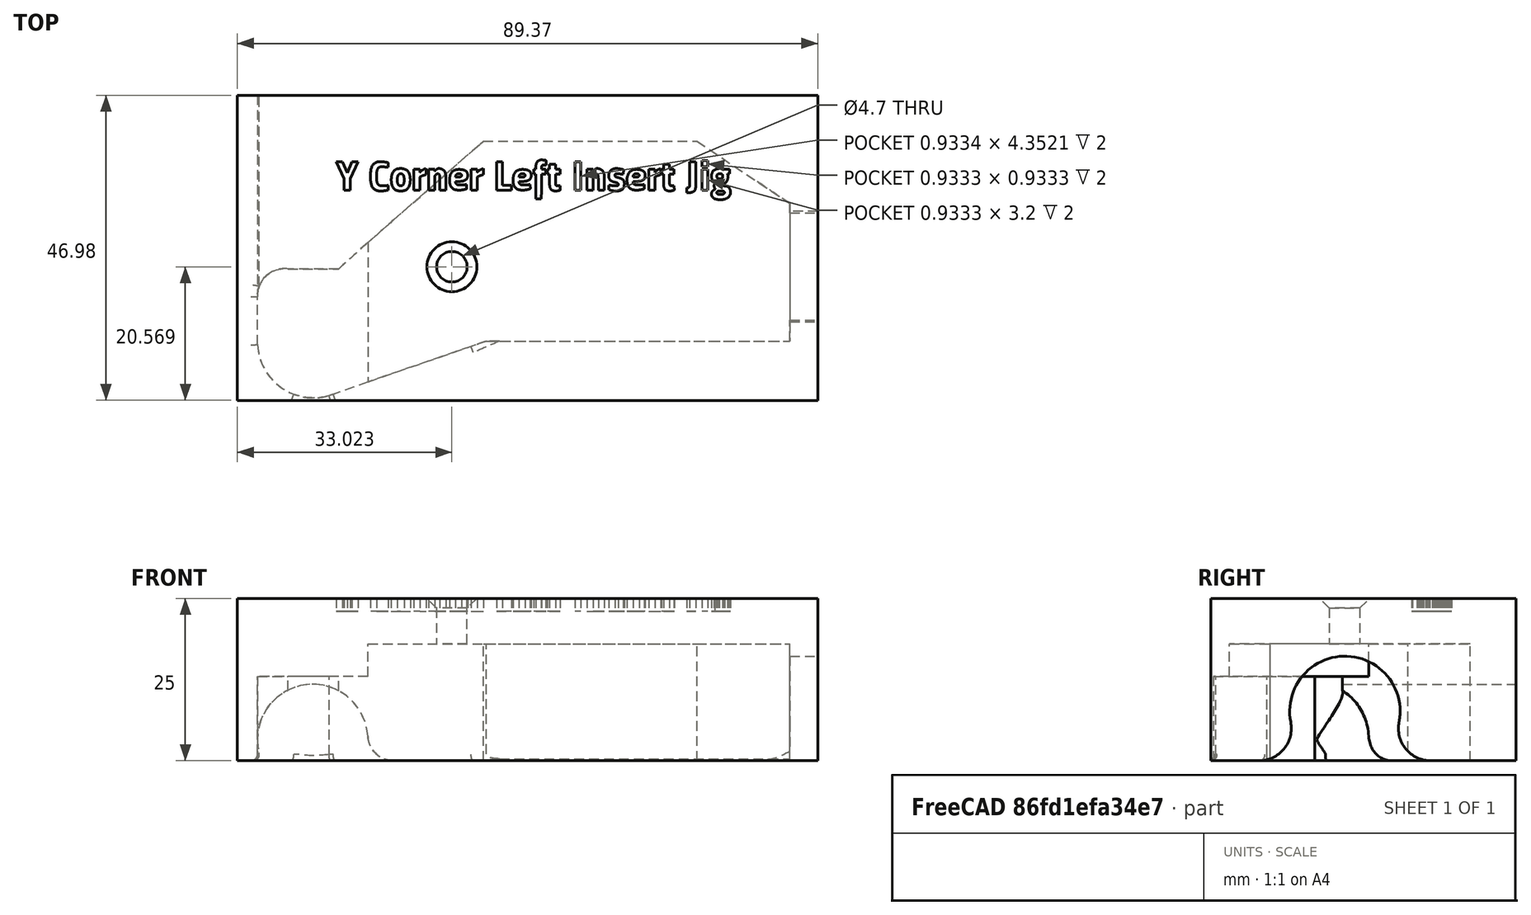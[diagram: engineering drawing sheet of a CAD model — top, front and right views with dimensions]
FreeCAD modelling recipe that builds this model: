
FCSTD DOCUMENT  (FreeCAD 0.17R9537 (Git))
Label: y_corner_left_insert_jig_m3
License: All rights reserved
LicenseURL: http://en.wikipedia.org/wiki/All_rights_reserved
objects: Sketcher::SketchObject×8, PartDesign::Pocket×6, PartDesign::Fillet×3, Mesh::Feature×1, PartDesign::Pad×1, Part::Feature×1, PartDesign::Plane×1, PartDesign::Chamfer×1, Part::Part2DObjectPython×1, PartDesign::Body×1
note: 30 computed .brp shape members not serialized (recipe doc carries the construction recipe); baked Part::Feature solids carry a one-line shape summary decoded from their .brp

FEATURE [Mesh::Feature] y_corner_left_v2_4  label="y_corner_left_v2.4"
  Placement = pos=(-95,-15,-13) rot=(0,0,1;0rad)
FEATURE [Sketcher::SketchObject] Sketch
  MapMode = 5
  Support = -> [XY_Plane]
  sketch-geometry (4):
    g0: LineSegment StartX=-41.2454 StartY=-29.3641 StartZ=0 EndX=48.1248 EndY=-29.3641 EndZ=0
    g1: LineSegment StartX=48.1248 StartY=-29.3641 StartZ=0 EndX=48.1248 EndY=17.6233 EndZ=0
    g2: LineSegment StartX=48.1248 StartY=17.6233 StartZ=0 EndX=-41.2454 EndY=17.6233 EndZ=0
    g3: LineSegment StartX=-41.2454 StartY=17.6233 StartZ=0 EndX=-41.2454 EndY=-29.3641 EndZ=0
  constraints (8):
    c: Coincident(g0,g1)
    c: Coincident(g1,g2)
    c: Coincident(g2,g3)
    c: Coincident(g3,g0)
    c: Horizontal(g0)
    c: Horizontal(g2)
    c: Vertical(g1)
    c: Vertical(g3)
FEATURE [PartDesign::Pad] Pad
  Length = 25
  Length2 = 100
  Profile = -> Sketch
  Type = 0
FEATURE [Part::Feature] y_corner_left_v2_4001
  Placement = pos=(0,0,12) rot=(0,0,1;0rad)
  shape: bbox 81.06 x 37.98 x 18.29 mm, 18592 faces, 0 solids (baked)
FEATURE [Sketcher::SketchObject] Sketch001
  MapMode = 5
  Placement = pos=(0,0,0) rot=(1,0,0;3.14159rad)
  Support = -> [Pad]
  sketch-geometry (7):
    g0: LineSegment StartX=-21.1438 StartY=5.05934 StartZ=0 EndX=-3.38972 EndY=-10.5427 EndZ=0
    g1: LineSegment StartX=-3.38972 StartY=-10.5427 StartZ=0 EndX=29.5098 EndY=-10.5427 EndZ=0
    g2: LineSegment StartX=29.5098 StartY=-10.5427 StartZ=0 EndX=43.8429 EndY=-0.932231 EndZ=0
    g3: LineSegment StartX=43.8429 StartY=-0.932231 StartZ=0 EndX=43.8429 EndY=20.2526 EndZ=0
    g4: LineSegment StartX=-21.1438 StartY=5.05934 StartZ=0 EndX=-21.1438 EndY=26.5193 EndZ=0
    g5: LineSegment StartX=-21.1438 StartY=26.5193 StartZ=0 EndX=-2.94605 EndY=20.2526 EndZ=0
    g6: LineSegment StartX=-2.94605 StartY=20.2526 StartZ=0 EndX=43.8429 EndY=20.2526 EndZ=0
  constraints (11):
    c: Coincident(g1,g0)
    c: Horizontal(g1)
    c: Coincident(g2,g1)
    c: Coincident(g3,g2)
    c: Vertical(g3)
    c: Coincident(g4,g0)
    c: Vertical(g4)
    c: Coincident(g5,g4)
    c: Coincident(g6,g5)
    c: Coincident(g6,g3)
    c: Horizontal(g6)
FEATURE [PartDesign::Pocket] Pocket
  BaseFeature = -> Pad
  Length = 18
  Profile = -> Sketch001
  Type = 0
FEATURE [Sketcher::SketchObject] Sketch002
  ExternalGeometry = -> [Pocket]
  MapMode = 5
  Placement = pos=(0,0,0) rot=(1,0,0;3.14159rad)
  Support = -> [Pocket]
  sketch-geometry (7):
    g0: LineSegment StartX=-21.1438 StartY=5.05934 StartZ=0 EndX=-25.6743 EndY=9.11448 EndZ=0
    g1: LineSegment StartX=-25.6743 StartY=9.11448 StartZ=0 EndX=-33.4497 EndY=9.11448 EndZ=0
    g2: LineSegment StartX=-21.1438 StartY=26.5193 StartZ=0 EndX=-27.1407 EndY=28.6513 EndZ=0
    g3: ArcOfCircle CenterX=-29.5136 CenterY=20.3238 CenterZ=0 NormalX=0 NormalY=0 NormalZ=1 Radius=8.65904 StartAngle=1.2932 EndAngle=3.08945
    g4: LineSegment StartX=-38.1609 StartY=20.7751 StartZ=0 EndX=-38.1609 EndY=13.4153 EndZ=0
    g5: ArcOfCircle CenterX=-33.9785 CenterY=13.266 CenterZ=0 NormalX=0 NormalY=0 NormalZ=1 Radius=4.18506 StartAngle=3.10591 EndAngle=4.83908
    g6: LineSegment StartX=-21.1438 StartY=5.05934 StartZ=0 EndX=-21.1438 EndY=26.5193 EndZ=0
  constraints (11):
    c: Coincident(g0,g-3)
    c: Coincident(g1,g0)
    c: Horizontal(g1)
    c: Coincident(g2,g-3)
    c: Coincident(g3,g2)
    c: Coincident(g4,g3)
    c: Vertical(g4)
    c: Coincident(g1,g5)
    c: Coincident(g4,g5)
    c: Coincident(g6,g0)
    c: Coincident(g6,g2)
FEATURE [PartDesign::Pocket] Pocket001
  BaseFeature = -> Pocket
  Length = 13
  Profile = -> Sketch002
  Type = 0
FEATURE [Sketcher::SketchObject] Sketch003
  MapMode = 5
  Placement = pos=(0,17.6233,0) rot=(0,0.707107,0.707107;3.14159rad)
  Support = -> [Pocket001]
  sketch-geometry (1):
    g0: Circle CenterX=29.6574 CenterY=3.27274 CenterZ=0 NormalX=0 NormalY=0 NormalZ=1 Radius=8.5
  constraints (1):
    c: Radius(g0) = 8.5
FEATURE [PartDesign::Pocket] Pocket002
  BaseFeature = -> Pocket001
  Length = 35
  Profile = -> Sketch003
  Type = 0
FEATURE [Sketcher::SketchObject] Sketch004
  MapMode = 5
  Placement = pos=(48.1248,0,0) rot=(0.57735,0.57735,0.57735;2.0944rad)
  Support = -> [Pocket002]
  sketch-geometry (1):
    g0: Circle CenterX=-8.75085 CenterY=7.61123 CenterZ=0 NormalX=0 NormalY=0 NormalZ=1 Radius=8.5
  constraints (1):
    c: Radius(g0) = 8.5
FEATURE [PartDesign::Pocket] Pocket003
  BaseFeature = -> Pocket002
  Length = 5
  Profile = -> Sketch004
  Type = 0
FEATURE [PartDesign::Fillet] Fillet
  Base = -> Pocket003 [Edge31,Edge23]
  BaseFeature = -> Pocket003
  Radius = 5
FEATURE [PartDesign::Fillet] Fillet001
  Base = -> Fillet [Edge43]
  BaseFeature = -> Fillet
  Radius = 4
FEATURE [PartDesign::Fillet] Fillet002
  Base = -> Fillet001 [Edge32,Edge41,Edge40,Edge38,Edge37,Edge35]
  BaseFeature = -> Fillet001
  Radius = 1
FEATURE [Sketcher::SketchObject] Sketch005
  ExternalGeometry = -> [y_corner_left_v2_4001,Fillet002]
  MapMode = 5
  Placement = pos=(0,-29.3641,0) rot=(1,0,0;1.5708rad)
  Support = -> [Fillet002]
  sketch-geometry (1):
    g0: LineSegment StartX=-26.1602 StartY=0 StartZ=0 EndX=-26.1602 EndY=-0.999892 EndZ=0
  constraints (3):
    c: Coincident(g0,g-4)
    c: PointOnObject(g0,g-3)
    c: Vertical(g0)
FEATURE [Sketcher::SketchObject] Sketch006
  MapMode = 5
  Placement = pos=(0,0,18) rot=(1,0,0;3.14159rad)
  Support = -> [Fillet002]
  sketch-geometry (1):
    g0: Circle CenterX=-8.22724 CenterY=8.79045 CenterZ=0 NormalX=0 NormalY=0 NormalZ=1 Radius=2.35
  constraints (1):
    c: Radius(g0) = 2.35
FEATURE [PartDesign::Pocket] Pocket004
  BaseFeature = -> Fillet002
  Length = 5
  Profile = -> Sketch006
  Type = 1
FEATURE [PartDesign::Plane] DatumPlane
  MapMode = 5
  Placement = pos=(0,0,10) rot=(1,0,0;3.14159rad)
  Support = -> [Pocket004]
  superPlacement = pos=(0,0,-10) rot=(0,0,1;0rad)
FEATURE [Sketcher::SketchObject] Sketch007
  ExternalGeometry = -> [Pocket004]
  MapMode = 5
  Placement = pos=(0,17.6233,0) rot=(0,0.707107,0.707107;3.14159rad)
  Support = -> [Pocket004]
  sketch-geometry (1):
    g0: LineSegment StartX=3.2818 StartY=25 StartZ=0 EndX=3.2818 EndY=9.8977 EndZ=0
  constraints (2):
    c: PointOnObject(g0,g-3)
    c: Vertical(g0)
FEATURE [PartDesign::Chamfer] Chamfer
  Base = -> Pocket004 [Edge37]
  BaseFeature = -> Pocket004
  Size = 1.5
FEATURE [Part::Part2DObjectPython] ShapeString  # Draft 2D object (typed FeaturePython)
  FontFile = <userpath>/Desktop/Titillium-BoldUpright.otf
  Placement = pos=(-26,3,25) rot=(0,0,1;0rad)
  Size = 2.5
  String = Y Corner Left Insert Jig
  Support = -> [Chamfer]
  Tracking = 70
FEATURE [PartDesign::Pocket] Pocket005
  BaseFeature = -> Chamfer
  Length = 2
  Profile = -> ShapeString
  Type = 0
FEATURE [PartDesign::Body] Body
  Model = -> [Sketch,Pad,Sketch001,Pocket,Sketch002,Pocket001,Sketch003,Pocket002,Sketch004,Pocket003,Fillet,Fillet001,Fillet002,Pocket004,DatumPlane,Sketch007,Chamfer,Pocket005]
  Origin = -> BodyOrigin
  Tip = -> Pocket005
